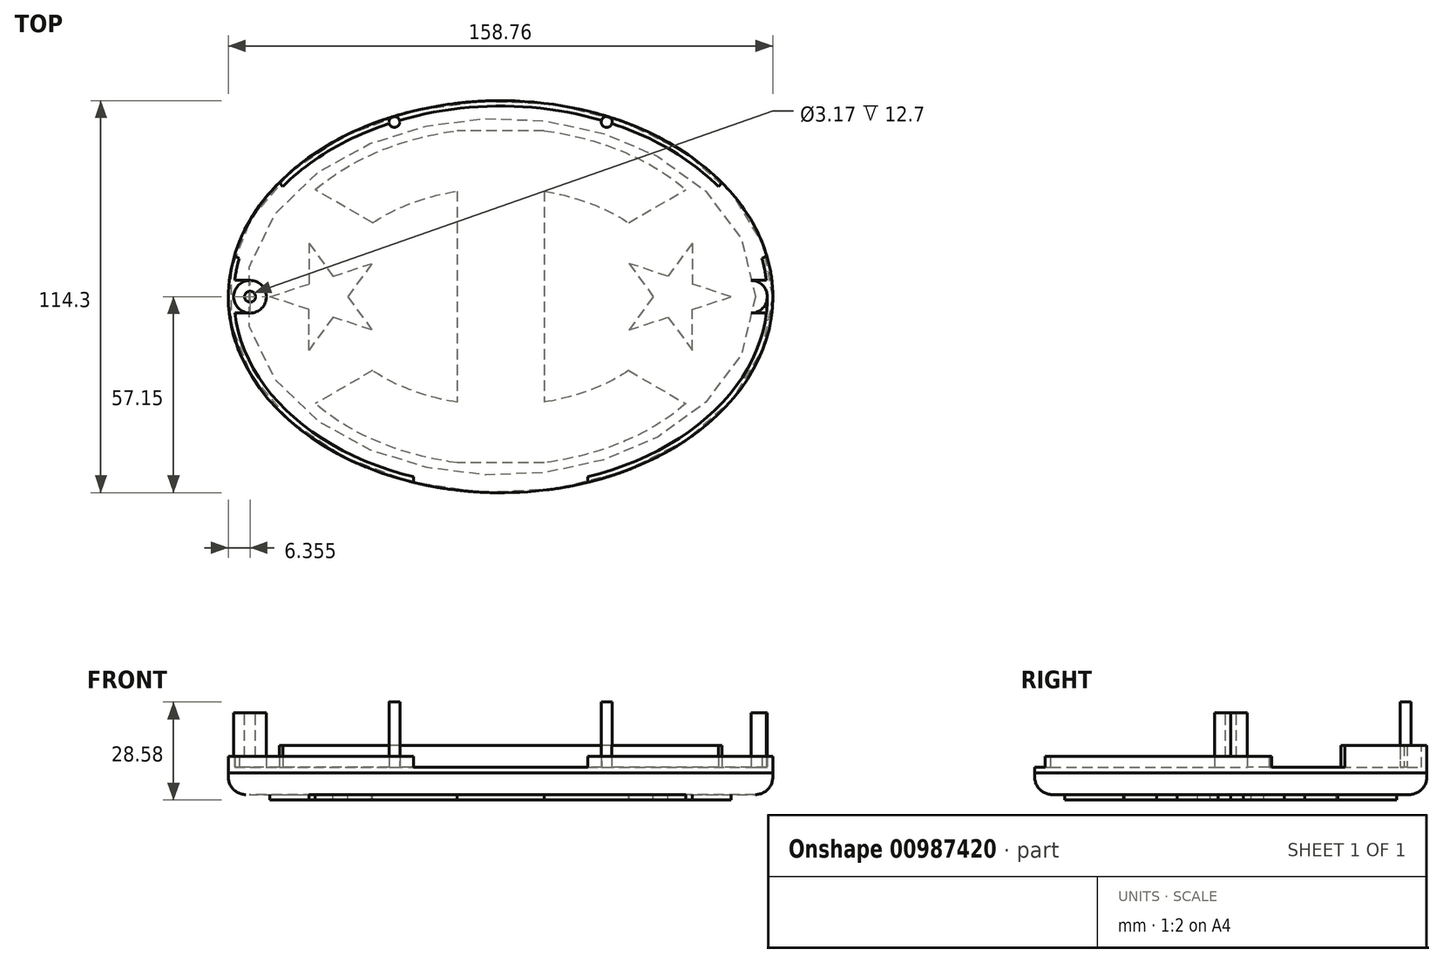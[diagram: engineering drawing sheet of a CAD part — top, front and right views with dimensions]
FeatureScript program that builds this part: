
annotation { "Feature Type Name" : "Feature", "Feature Type Description" : "" }
export const myFeature = defineFeature(function(context is Context, id is Id, definition is map)
    precondition{}
    {
        {
            var Q0;
            Q0=qCreatedBy(makeId("Top.planeOp"),FACE);
            var sketch = newSketch(context, id + "F0", { "sketchPlane" : qUnion([Q0])});
            skEllipse(sketch, "E0", {"center": v(0, 0) * mm, "majorRadius": 79.38 * mm, "minorRadius": 57.15 * mm, "majorAxis": v(1, 0)});
            skSolve(sketch);
        }
        {
            var Q0;
            Q0=makeQuery(id+"F0.imprint","IMPRINT",FACE,{"disambiguationData":[TD([[makeQuery(id+"F0.imprint","IMPRINT",EDGE,{"derivedFrom":sQuery(id+"F0.wireOp",EDGE,"E0")}),1.0]])]});
            extrude(context, id + "F1", {"entities" : qUnion([Q0]), "depth" : 1.59 * mm, "offsetDistance" : 25.4 * mm});
        }
        {
            var Q0;
            Q0=makeQuery(id+"F1.opExtrude","CAP_FACE",FACE,{"disambiguationData":[OSD([sQuery(id+"F0.wireOp",EDGE,"E0")])],"isStart":false});
            var sketch = newSketch(context, id + "F2", { "sketchPlane" : qUnion([Q0])});
            skEllipse(sketch, "E1", {"center": v(0, 0) * mm, "majorRadius": 77.79 * mm, "minorRadius": 55.56 * mm, "majorAxis": v(1, 0)});
            skLineSegment(sketch, "E2", {"start": v(-25.4, -54.14) * mm, "end": v(25.4, -54.14) * mm});
            skLineSegment(sketch, "E3", {"start": v(-25.4, -54.14) * mm, "end": v(-25.4, -52.52) * mm});
            skLineSegment(sketch, "E4", {"start": v(25.4, -54.14) * mm, "end": v(25.4, -52.52) * mm});
            skLineSegment(sketch, "E5", {"start": v(-63.5, 32.1) * mm, "end": v(63.5, 32.1) * mm});
            skLineSegment(sketch, "E6", {"start": v(-64.51, 33.3) * mm, "end": v(-63.5, 32.1) * mm});
            skLineSegment(sketch, "E7", {"start": v(63.5, 32.1) * mm, "end": v(64.51, 33.3) * mm});
            skLineSegment(sketch, "E8", {"start": v(-76.2, 11.17) * mm, "end": v(76.2, 11.17) * mm});
            skLineSegment(sketch, "E9", {"start": v(-76.2, 11.17) * mm, "end": v(-77.61, 11.98) * mm});
            skLineSegment(sketch, "E10", {"start": v(76.2, 11.17) * mm, "end": v(77.61, 11.98) * mm});
            skSolve(sketch);
        }
        {
            var Q0;
            {var subQ0=sQuery(id+"F2.wireOp",EDGE,"E3");Q0=makeQuery(id+"F2.imprint","IMPRINT",FACE,{"disambiguationData":[TD([[makeQuery(id+"F2.imprint","IMPRINT",EDGE,{"derivedFrom":subQ0}),1.0]])]});}
            var Q1;
            {var subQ0=sQuery(id+"F2.wireOp",EDGE,"E4");Q1=makeQuery(id+"F2.imprint","IMPRINT",FACE,{"disambiguationData":[TD([[makeQuery(id+"F2.imprint","IMPRINT",EDGE,{"derivedFrom":subQ0}),-1.0]])]});}
            extrude(context, id + "F3", {"entities" : qUnion([Q0, Q1]), "operationType" : NewBodyOperationType.ADD, "depth" : 3.17 * mm, "offsetDistance" : 25.4 * mm});
        }
        {
            var Q0;
            {var subQ0=sQuery(id+"F2.wireOp",EDGE,"E6");Q0=makeQuery(id+"F2.imprint","IMPRINT",FACE,{"disambiguationData":[TD([[makeQuery(id+"F2.imprint","IMPRINT",EDGE,{"derivedFrom":subQ0}),1.0]])]});}
            extrude(context, id + "F4", {"entities" : qUnion([Q0]), "operationType" : NewBodyOperationType.ADD, "depth" : 6.35 * mm, "offsetDistance" : 25.4 * mm});
        }
        {
            var Q0;
            Q0=makeQuery(id+"F1.opExtrude","CAP_FACE",FACE,{"disambiguationData":[OSD([sQuery(id+"F0.wireOp",EDGE,"E0")])],"isStart":false});
            var sketch = newSketch(context, id + "F5", { "sketchPlane" : qUnion([Q0])});
            skCircle(sketch, "E11", {"center": v(-30.96, 50.96) * mm, "radius": 1.59 * mm});
            skCircle(sketch, "E12", {"center": v(30.96, 50.96) * mm, "radius": 1.59 * mm});
            skPoint(sketch, "E13", {"position": v(-32.54, 50.96) * mm});
            skPoint(sketch, "E14", {"position": v(32.54, 50.96) * mm});
            skLineSegment(sketch, "E15", {"start": v(-30.96, 50.96) * mm, "end": v(30.96, 50.96) * mm, "construction": true});
            skPoint(sketch, "E16", {"position": v(0, 50.96) * mm});
            skSolve(sketch);
        }
        {
            var Q0;
            {var subQ0=sQuery(id+"F5.wireOp",EDGE,"E11");var subQ1=makeQuery(id+"F4.opExtrude","CAP_EDGE",EDGE,{"disambiguationData":[OSD([sQuery(id+"F2.wireOp",EDGE,"E1")])],"isStart":true});var subQ2=makeQuery(id+"F5.imprint","INTERSECT",VERTEX,{"disambiguationData":[OD(0.0)],"derivedFrom":[subQ1,subQ0]});Q0=makeQuery(id+"F5.imprint","IMPRINT",FACE,{"disambiguationData":[TD([[makeQuery(id+"F5.imprint","IMPRINT",EDGE,{"disambiguationData":[TD([[subQ2,-1.0]])],"derivedFrom":subQ0}),1.0]])]});}
            var Q1;
            {var subQ0=sQuery(id+"F5.wireOp",EDGE,"E12");var subQ1=makeQuery(id+"F4.opExtrude","CAP_EDGE",EDGE,{"disambiguationData":[OSD([sQuery(id+"F2.wireOp",EDGE,"E1")])],"isStart":true});var subQ2=makeQuery(id+"F5.imprint","INTERSECT",VERTEX,{"disambiguationData":[OD(0.0)],"derivedFrom":[subQ1,subQ0]});Q1=makeQuery(id+"F5.imprint","IMPRINT",FACE,{"disambiguationData":[TD([[makeQuery(id+"F5.imprint","IMPRINT",EDGE,{"disambiguationData":[TD([[subQ2,1.0]])],"derivedFrom":subQ0}),1.0]])]});}
            var Q2;
            {var subQ0=sQuery(id+"F5.wireOp",EDGE,"E11");var subQ1=makeQuery(id+"F4.opExtrude","CAP_EDGE",EDGE,{"disambiguationData":[OSD([sQuery(id+"F2.wireOp",EDGE,"E1")])],"isStart":true});var subQ2=makeQuery(id+"F5.imprint","INTERSECT",VERTEX,{"disambiguationData":[OD(0.0)],"derivedFrom":[subQ1,subQ0]});Q2=makeQuery(id+"F5.imprint","IMPRINT",FACE,{"disambiguationData":[TD([[makeQuery(id+"F5.imprint","IMPRINT",EDGE,{"disambiguationData":[TD([[subQ2,1.0]])],"derivedFrom":subQ0}),1.0]])]});}
            var Q3;
            {var subQ0=sQuery(id+"F5.wireOp",EDGE,"E12");var subQ1=makeQuery(id+"F4.opExtrude","CAP_EDGE",EDGE,{"disambiguationData":[OSD([sQuery(id+"F2.wireOp",EDGE,"E1")])],"isStart":true});var subQ2=makeQuery(id+"F5.imprint","INTERSECT",VERTEX,{"disambiguationData":[OD(0.0)],"derivedFrom":[subQ1,subQ0]});Q3=makeQuery(id+"F5.imprint","IMPRINT",FACE,{"disambiguationData":[TD([[makeQuery(id+"F5.imprint","IMPRINT",EDGE,{"disambiguationData":[TD([[subQ2,-1.0]])],"derivedFrom":subQ0}),1.0]])]});}
            extrude(context, id + "F6", {"entities" : qUnion([Q0, Q1, Q2, Q3]), "operationType" : NewBodyOperationType.ADD, "depth" : 19.05 * mm, "offsetDistance" : 25.4 * mm});
        }
        {
            var Q0;
            Q0=makeQuery(id+"F1.opExtrude","CAP_FACE",FACE,{"disambiguationData":[OSD([sQuery(id+"F0.wireOp",EDGE,"E0")])],"isStart":false});
            var sketch = newSketch(context, id + "F7", { "sketchPlane" : qUnion([Q0])});
            skCircle(sketch, "E17", {"center": v(-73.03, 0) * mm, "radius": 4.76 * mm});
            skLineSegment(sketch, "E18", {"start": v(-73.03, -4.76) * mm, "end": v(-77.5, -4.76) * mm});
            skLineSegment(sketch, "E19", {"start": v(-73.03, 4.76) * mm, "end": v(-77.5, 4.76) * mm});
            skEllipticalArc(sketch, "E20.0", {});
            skPoint(sketch, "E21.orphan", {"position": v(-76.2, 11.17) * mm});
            skPoint(sketch, "E22.orphan", {"position": v(-25.4, -52.52) * mm});
            skLineSegment(sketch, "E23", {"start": v(0, 0) * mm, "end": v(0, 25.4) * mm, "construction": true});
            skEllipticalArc(sketch, "E24.MirrorCS", {});
            skLineSegment(sketch, "E25.MirrorCS", {"start": v(73.03, 4.76) * mm, "end": v(77.5, 4.76) * mm});
            skCircle(sketch, "E26.MirrorC", {"center": v(73.03, 0) * mm, "radius": 4.76 * mm});
            skLineSegment(sketch, "E27.MirrorCS", {"start": v(73.03, -4.76) * mm, "end": v(77.5, -4.76) * mm});
            const initialGuessF7  = {"E20.0": [0, 0, 1, 0, 0.07778750000000001, 0.05556250000000001, 3.0557730630838975, 3.2274122440956874], "E24.MirrorCS": [0, 0, -1, 0, 0.07778750000000001, 0.05556250000000001, 3.0557730630838993, 3.2274122440956887]};
            skSetInitialGuess(sketch, initialGuessF7);
            skSolve(sketch);
        }
        {
            var Q0;
            {var subQ0=sQuery(id+"F7.wireOp",EDGE,"E19");Q0=makeQuery(id+"F7.imprint","IMPRINT",FACE,{"disambiguationData":[TD([[makeQuery(id+"F7.imprint","IMPRINT",EDGE,{"derivedFrom":subQ0}),1.0]])]});}
            var Q1;
            {var subQ0=sQuery(id+"F7.wireOp",EDGE,"E18");Q1=makeQuery(id+"F7.imprint","IMPRINT",FACE,{"disambiguationData":[TD([[makeQuery(id+"F7.imprint","IMPRINT",EDGE,{"derivedFrom":subQ0}),-1.0]])]});}
            var Q2;
            {var subQ0=sQuery(id+"F7.wireOp",EDGE,"E17");var subQ1=makeQuery(id+"F7.imprint","INTERSECT",VERTEX,{"derivedFrom":[subQ0,sQuery(id+"F7.wireOp",EDGE,"E19")]});Q2=makeQuery(id+"F7.imprint","IMPRINT",FACE,{"disambiguationData":[TD([[makeQuery(id+"F7.imprint","IMPRINT",EDGE,{"disambiguationData":[TD([[subQ1,-1.0]])],"derivedFrom":subQ0}),1.0]])]});}
            var Q3;
            {var subQ0=sQuery(id+"F7.wireOp",EDGE,"E26.MirrorC");var subQ1=makeQuery(id+"F7.imprint","INTERSECT",VERTEX,{"derivedFrom":[sQuery(id+"F7.wireOp",EDGE,"E24.MirrorCS"),subQ0]});Q3=makeQuery(id+"F7.imprint","IMPRINT",FACE,{"disambiguationData":[TD([[makeQuery(id+"F7.imprint","IMPRINT",EDGE,{"disambiguationData":[TD([[subQ1,1.0]])],"derivedFrom":subQ0}),-1.0]])]});}
            var Q4;
            {var subQ3=sQuery(id+"F7.wireOp",EDGE,"E25.MirrorCS");Q4=makeQuery(id+"F7.imprint","IMPRINT",FACE,{"disambiguationData":[TD([[makeQuery(id+"F7.imprint","IMPRINT",EDGE,{"derivedFrom":subQ3}),-1.0]])]});}
            var Q5;
            {var subQ3=sQuery(id+"F7.wireOp",EDGE,"E27.MirrorCS");Q5=makeQuery(id+"F7.imprint","IMPRINT",FACE,{"disambiguationData":[TD([[makeQuery(id+"F7.imprint","IMPRINT",EDGE,{"derivedFrom":subQ3}),1.0]])]});}
            extrude(context, id + "F8", {"entities" : qUnion([Q0, Q1, Q2, Q3, Q4, Q5]), "operationType" : NewBodyOperationType.ADD, "depth" : 3.17 * mm, "offsetDistance" : 25.4 * mm});
        }
        {
            var Q0;
            {var subQ0=sQuery(id+"F7.wireOp",EDGE,"E17");var subQ1=makeQuery(id+"F7.imprint","INTERSECT",VERTEX,{"derivedFrom":[subQ0,sQuery(id+"F7.wireOp",EDGE,"E19")]});Q0=makeQuery(id+"F7.imprint","IMPRINT",FACE,{"disambiguationData":[TD([[makeQuery(id+"F7.imprint","IMPRINT",EDGE,{"disambiguationData":[TD([[subQ1,-1.0]])],"derivedFrom":subQ0}),1.0]])]});}
            var Q1;
            {var subQ0=sQuery(id+"F7.wireOp",EDGE,"E26.MirrorC");var subQ1=makeQuery(id+"F7.imprint","INTERSECT",VERTEX,{"derivedFrom":[sQuery(id+"F7.wireOp",EDGE,"E24.MirrorCS"),subQ0]});Q1=makeQuery(id+"F7.imprint","IMPRINT",FACE,{"disambiguationData":[TD([[makeQuery(id+"F7.imprint","IMPRINT",EDGE,{"disambiguationData":[TD([[subQ1,1.0]])],"derivedFrom":subQ0}),-1.0]])]});}
            extrude(context, id + "F9", {"entities" : qUnion([Q0, Q1]), "operationType" : NewBodyOperationType.ADD, "depth" : 15.88 * mm, "offsetDistance" : 25.4 * mm});
        }
        {
            var Q0;
            Q0=makeQuery(id+"F9.opExtrude","CAP_FACE",FACE,{"disambiguationData":[OSD([sQuery(id+"F7.wireOp",EDGE,"E17")])],"isStart":false});
            var sketch = newSketch(context, id + "F10", { "sketchPlane" : qUnion([Q0])});
            skCircle(sketch, "E28", {"center": v(-73.03, 0) * mm, "radius": 1.59 * mm});
            skPoint(sketch, "E29", {"position": v(73.03, 0) * mm});
            skCircle(sketch, "E30", {"center": v(73.03, 0) * mm, "radius": 1.59 * mm});
            skSolve(sketch);
        }
        {
            var Q0;
            Q0=makeQuery(id+"F10.imprint","IMPRINT",FACE,{"disambiguationData":[TD([[makeQuery(id+"F10.imprint","IMPRINT",EDGE,{"derivedFrom":sQuery(id+"F10.wireOp",EDGE,"E28")}),1.0]])]});
            var Q1;
            Q1=makeQuery(id+"F10.imprint","IMPRINT",FACE,{"disambiguationData":[TD([[makeQuery(id+"F10.imprint","IMPRINT",EDGE,{"derivedFrom":sQuery(id+"F10.wireOp",EDGE,"E30")}),1.0]])]});
            extrude(context, id + "F11", {"entities" : qUnion([Q0, Q1]), "operationType" : NewBodyOperationType.REMOVE, "oppositeDirection" : true, "depth" : 12.7 * mm, "offsetDistance" : 25.4 * mm});
        }
        {
            var Q0;
            Q0=makeQuery(id+"F1.opExtrude","CAP_FACE",FACE,{"disambiguationData":[OSD([sQuery(id+"F0.wireOp",EDGE,"E0")])],"isStart":true});
            var sketch = newSketch(context, id + "F12", { "sketchPlane" : qUnion([Q0])});
            skEllipse(sketch, "E31.0.0", {"center": v(0, 0) * mm, "majorRadius": 79.38 * mm, "minorRadius": 57.15 * mm, "majorAxis": v(1, 0)});
            skSolve(sketch);
        }
        {
            var Q0;
            Q0 = qSketchRegion(id + "F12", true);
            extrude(context, id + "F13", {"entities" : qUnion([Q0]), "depth" : 6.35 * mm, "offsetDistance" : 25.4 * mm});
        }
        {
            var Q0;
            Q0=makeQuery(id+"F13.opExtrude","CAP_EDGE",EDGE,{"disambiguationData":[OSD([sQuery(id+"F12.wireOp",EDGE,"E31.0.0")])],"isStart":false});
            fillet(context, id + "F14", {"entities" : qUnion([Q0]), "radius" : 5.08 * mm, "tangentPropagation" : true, "allowEdgeOverflow" : false});
        }
        {
            var Q0;
            Q0=makeQuery(id+"F13.opExtrude","CAP_FACE",FACE,{"disambiguationData":[OSD([sQuery(id+"F12.wireOp",EDGE,"E31.0.0")])],"isStart":false});
            var sketch = newSketch(context, id + "F15", { "sketchPlane" : qUnion([Q0])});
            skPoint(sketch, "E32", {"position": v(34.39, 39.1) * mm});
            skPoint(sketch, "E33", {"position": v(38.93, 32.43) * mm});
            skPoint(sketch, "E34", {"position": v(42, 25.2) * mm});
            skPoint(sketch, "E35", {"position": v(44.9, 15.35) * mm});
            skPoint(sketch, "E36", {"position": v(46.32, 4.56) * mm});
            skPoint(sketch, "E37", {"position": v(47.2, -7.17) * mm});
            skPoint(sketch, "E38", {"position": v(46.9, -15.38) * mm});
            skPoint(sketch, "E39", {"position": v(44.76, -23.97) * mm});
            skPoint(sketch, "E40", {"position": v(41.67, -31.08) * mm});
            skPoint(sketch, "E41", {"position": v(37.64, -37.83) * mm});
            skPoint(sketch, "E42", {"position": v(30.8, -44.05) * mm});
            skPoint(sketch, "E43", {"position": v(23.18, -46) * mm});
            skPoint(sketch, "E44", {"position": v(13.85, -46) * mm});
            skPoint(sketch, "E45", {"position": v(8.76, -41.5) * mm});
            skPoint(sketch, "E46", {"position": v(7.4, -35.36) * mm});
            skPoint(sketch, "E47", {"position": v(9.76, -29.55) * mm});
            skPoint(sketch, "E48", {"position": v(15.32, -26.33) * mm});
            skPoint(sketch, "E49", {"position": v(19.78, -25.54) * mm});
            skPoint(sketch, "E50", {"position": v(25.57, -25.66) * mm});
            skPoint(sketch, "E51", {"position": v(28.75, -26.93) * mm});
            skPoint(sketch, "E52", {"position": v(31, -27.28) * mm});
            skPoint(sketch, "E53", {"position": v(32.82, -23.72) * mm});
            skPoint(sketch, "E54", {"position": v(34.06, -17.75) * mm});
            skPoint(sketch, "E55", {"position": v(34.2, -12.9) * mm});
            skPoint(sketch, "E56", {"position": v(33.4, -8.8) * mm});
            skPoint(sketch, "E57", {"position": v(32.06, -4.72) * mm});
            skPoint(sketch, "E58", {"position": v(29.94, 1.22) * mm});
            skPoint(sketch, "E59", {"position": v(26.93, 3.42) * mm});
            skPoint(sketch, "E60", {"position": v(23.18, -0.34) * mm});
            skPoint(sketch, "E61", {"position": v(18.25, -4.3) * mm});
            skPoint(sketch, "E62", {"position": v(11.38, -7.18) * mm});
            skPoint(sketch, "E63", {"position": v(3.38, -9.12) * mm});
            skPoint(sketch, "E64", {"position": v(-4.82, -9.77) * mm});
            skPoint(sketch, "E65", {"position": v(-12.3, -7.98) * mm});
            skPoint(sketch, "E66", {"position": v(-16.8, -6.35) * mm});
            skPoint(sketch, "E67", {"position": v(-21.69, 0) * mm});
            skPoint(sketch, "E68", {"position": v(-25.84, 2.12) * mm});
            skPoint(sketch, "E69", {"position": v(-29.04, 4.51) * mm});
            skPoint(sketch, "E70", {"position": v(-35.39, 5.56) * mm});
            skPoint(sketch, "E71", {"position": v(-32.97, 23.1) * mm});
            skPoint(sketch, "E72", {"position": v(-30.19, 24.81) * mm});
            skPoint(sketch, "E73", {"position": v(-28.56, 29.86) * mm});
            skPoint(sketch, "E74", {"position": v(-30.19, 34.33) * mm});
            skPoint(sketch, "E75", {"position": v(-32.97, 38.96) * mm});
            skPoint(sketch, "E76", {"position": v(-32.53, 43.33) * mm});
            skPoint(sketch, "E77", {"position": v(-28.9, 44.58) * mm});
            skPoint(sketch, "E78", {"position": v(31.7, 41.92) * mm});
            skPoint(sketch, "E79", {"position": v(26.4, 43.84) * mm});
            skPoint(sketch, "E80", {"position": v(21.5, 45.23) * mm});
            skPoint(sketch, "E81", {"position": v(18.62, 44.02) * mm});
            skPoint(sketch, "E82", {"position": v(17.5, 38.08) * mm});
            skPoint(sketch, "E83", {"position": v(17.67, 34) * mm});
            skPoint(sketch, "E84", {"position": v(18.78, 28.47) * mm});
            skPoint(sketch, "E85", {"position": v(18.02, 25.57) * mm});
            skPoint(sketch, "E86", {"position": v(14.3, 28.03) * mm});
            skPoint(sketch, "E87", {"position": v(9.27, 29.95) * mm});
            skPoint(sketch, "E88", {"position": v(4.38, 31.09) * mm});
            skPoint(sketch, "E89", {"position": v(0, 31.56) * mm});
            skPoint(sketch, "E90", {"position": v(-6.97, 31.63) * mm});
            skPoint(sketch, "E91", {"position": v(-12.9, 31.04) * mm});
            skPoint(sketch, "E92", {"position": v(-20.98, 46.24) * mm});
            skPoint(sketch, "E93", {"position": v(-17.93, 45.22) * mm});
            skPoint(sketch, "E94", {"position": v(-14.43, 38.66) * mm});
            skPoint(sketch, "E95", {"position": v(-25.26, 45.9) * mm});
            skPoint(sketch, "E96", {"position": v(-37.95, 1.3) * mm});
            skPoint(sketch, "E97", {"position": v(-38.05, -14) * mm});
            skPoint(sketch, "E98", {"position": v(-34.8, -21.34) * mm});
            skPoint(sketch, "E99", {"position": v(-48.3, -16.47) * mm});
            skPoint(sketch, "E100", {"position": v(-49.5, 0) * mm});
            skPoint(sketch, "E101", {"position": v(-47.8, 10.15) * mm});
            skPoint(sketch, "E102", {"position": v(-42.09, 18.38) * mm});
            skPoint(sketch, "E103", {"position": v(-39.71, -6.63) * mm});
            skPoint(sketch, "E104", {"position": v(-42.13, -28.7) * mm});
            skPoint(sketch, "E105", {"position": v(-33.45, -37.55) * mm});
            skPoint(sketch, "E106", {"position": v(-30.65, -37.9) * mm});
            skPoint(sketch, "E107", {"position": v(-29, -36) * mm});
            skPoint(sketch, "E108", {"position": v(-32.07, -27.28) * mm});
            skLineSegment(sketch, "E109", {"start": v(37.64, -37.83) * mm, "end": v(41.67, -31.08) * mm});
            skLineSegment(sketch, "E110", {"start": v(44.76, -23.97) * mm, "end": v(46.9, -15.38) * mm});
            skLineSegment(sketch, "E111", {"start": v(47.2, -7.17) * mm, "end": v(46.32, 4.56) * mm});
            skLineSegment(sketch, "E112", {"start": v(44.9, 15.35) * mm, "end": v(42, 25.2) * mm});
            skLineSegment(sketch, "E113", {"start": v(44.9, 15.35) * mm, "end": v(46.32, 4.56) * mm});
            skLineSegment(sketch, "E114", {"start": v(47.2, -7.17) * mm, "end": v(46.9, -15.38) * mm});
            skLineSegment(sketch, "E115", {"start": v(44.76, -23.97) * mm, "end": v(41.67, -31.08) * mm});
            skLineSegment(sketch, "E116", {"start": v(37.64, -37.83) * mm, "end": v(30.8, -44.05) * mm});
            skLineSegment(sketch, "E117", {"start": v(30.8, -44.05) * mm, "end": v(23.18, -46) * mm});
            skLineSegment(sketch, "E118", {"start": v(23.18, -46) * mm, "end": v(13.85, -46) * mm});
            skLineSegment(sketch, "E119", {"start": v(13.85, -46) * mm, "end": v(8.76, -41.5) * mm});
            skLineSegment(sketch, "E120", {"start": v(8.76, -41.5) * mm, "end": v(7.4, -35.36) * mm});
            skLineSegment(sketch, "E121", {"start": v(7.4, -35.36) * mm, "end": v(9.76, -29.55) * mm});
            skLineSegment(sketch, "E122", {"start": v(9.76, -29.55) * mm, "end": v(15.32, -26.33) * mm});
            skLineSegment(sketch, "E123", {"start": v(19.78, -25.54) * mm, "end": v(15.32, -26.33) * mm});
            skLineSegment(sketch, "E124", {"start": v(19.78, -25.54) * mm, "end": v(25.57, -25.66) * mm});
            skLineSegment(sketch, "E125", {"start": v(28.75, -26.93) * mm, "end": v(25.57, -25.66) * mm});
            skLineSegment(sketch, "E126", {"start": v(28.75, -26.93) * mm, "end": v(31, -27.28) * mm});
            skLineSegment(sketch, "E127", {"start": v(31, -27.28) * mm, "end": v(32.82, -23.72) * mm});
            skLineSegment(sketch, "E128", {"start": v(32.82, -23.72) * mm, "end": v(34.06, -17.75) * mm});
            skLineSegment(sketch, "E129", {"start": v(34.06, -17.75) * mm, "end": v(34.2, -12.9) * mm});
            skLineSegment(sketch, "E130", {"start": v(33.4, -8.8) * mm, "end": v(34.2, -12.9) * mm});
            skLineSegment(sketch, "E131", {"start": v(33.4, -8.8) * mm, "end": v(32.06, -4.72) * mm});
            skLineSegment(sketch, "E132", {"start": v(32.06, -4.72) * mm, "end": v(29.94, 1.22) * mm});
            skLineSegment(sketch, "E133", {"start": v(29.94, 1.22) * mm, "end": v(26.93, 3.42) * mm});
            skLineSegment(sketch, "E134", {"start": v(26.93, 3.42) * mm, "end": v(23.18, -0.34) * mm});
            skLineSegment(sketch, "E135", {"start": v(23.18, -0.34) * mm, "end": v(18.25, -4.3) * mm});
            skLineSegment(sketch, "E136", {"start": v(18.25, -4.3) * mm, "end": v(11.38, -7.18) * mm});
            skLineSegment(sketch, "E137", {"start": v(3.38, -9.12) * mm, "end": v(11.38, -7.18) * mm});
            skLineSegment(sketch, "E138", {"start": v(3.38, -9.12) * mm, "end": v(-4.82, -9.77) * mm});
            skLineSegment(sketch, "E139", {"start": v(-4.82, -9.77) * mm, "end": v(-12.3, -7.98) * mm});
            skLineSegment(sketch, "E140", {"start": v(-12.3, -8) * mm, "end": v(-16.8, -6.35) * mm});
            skLineSegment(sketch, "E141", {"start": v(-21.69, 0) * mm, "end": v(-16.8, -6.35) * mm});
            skLineSegment(sketch, "E142", {"start": v(-21.69, 0) * mm, "end": v(-25.84, 2.12) * mm});
            skLineSegment(sketch, "E143", {"start": v(-25.84, 2.12) * mm, "end": v(-29.04, 4.51) * mm});
            skLineSegment(sketch, "E144", {"start": v(-35.39, 5.56) * mm, "end": v(-37.95, 1.3) * mm});
            skLineSegment(sketch, "E145", {"start": v(-39.71, -6.63) * mm, "end": v(-38.05, -14) * mm});
            skLineSegment(sketch, "E146", {"start": v(-34.8, -21.34) * mm, "end": v(-32.07, -27.28) * mm});
            skLineSegment(sketch, "E147", {"start": v(-29, -36) * mm, "end": v(-30.65, -37.9) * mm});
            skLineSegment(sketch, "E148", {"start": v(-33.45, -37.55) * mm, "end": v(-42.13, -28.7) * mm});
            skLineSegment(sketch, "E149", {"start": v(-48.3, -16.47) * mm, "end": v(-49.5, 0) * mm});
            skLineSegment(sketch, "E150", {"start": v(-47.8, 10.15) * mm, "end": v(-42.09, 18.38) * mm});
            skLineSegment(sketch, "E151", {"start": v(-47.8, 10.15) * mm, "end": v(-49.5, 0) * mm});
            skLineSegment(sketch, "E152", {"start": v(-37.95, 1.3) * mm, "end": v(-39.71, -6.63) * mm});
            skLineSegment(sketch, "E153", {"start": v(-38.05, -14) * mm, "end": v(-34.8, -21.34) * mm});
            skLineSegment(sketch, "E154", {"start": v(-32.07, -27.28) * mm, "end": v(-29, -36) * mm});
            skLineSegment(sketch, "E155", {"start": v(-30.65, -37.9) * mm, "end": v(-33.45, -37.55) * mm});
            skLineSegment(sketch, "E156", {"start": v(-42.13, -28.7) * mm, "end": v(-48.3, -16.47) * mm});
            skLineSegment(sketch, "E157", {"start": v(42, 25.2) * mm, "end": v(38.93, 32.43) * mm});
            skLineSegment(sketch, "E158", {"start": v(34.39, 39.1) * mm, "end": v(31.7, 41.92) * mm});
            skLineSegment(sketch, "E159", {"start": v(26.4, 43.84) * mm, "end": v(21.5, 45.23) * mm});
            skLineSegment(sketch, "E160", {"start": v(18.62, 44.02) * mm, "end": v(17.5, 38.08) * mm});
            skLineSegment(sketch, "E161", {"start": v(17.67, 34) * mm, "end": v(18.78, 28.47) * mm});
            skLineSegment(sketch, "E162", {"start": v(18.02, 25.57) * mm, "end": v(14.3, 28.03) * mm});
            skLineSegment(sketch, "E163", {"start": v(9.27, 29.95) * mm, "end": v(4.38, 31.09) * mm});
            skLineSegment(sketch, "E164", {"start": v(0, 31.56) * mm, "end": v(-6.97, 31.63) * mm});
            skLineSegment(sketch, "E165", {"start": v(-14.43, 38.66) * mm, "end": v(-17.93, 45.22) * mm});
            skLineSegment(sketch, "E166", {"start": v(-6.97, 31.63) * mm, "end": v(-12.9, 31.04) * mm});
            skLineSegment(sketch, "E167", {"start": v(0, 31.56) * mm, "end": v(4.38, 31.09) * mm});
            skLineSegment(sketch, "E168", {"start": v(9.27, 29.95) * mm, "end": v(14.3, 28.03) * mm});
            skLineSegment(sketch, "E169", {"start": v(18.02, 25.57) * mm, "end": v(18.78, 28.47) * mm});
            skLineSegment(sketch, "E170", {"start": v(17.67, 34) * mm, "end": v(17.5, 38.08) * mm});
            skLineSegment(sketch, "E171", {"start": v(18.62, 44.02) * mm, "end": v(21.5, 45.23) * mm});
            skLineSegment(sketch, "E172", {"start": v(26.4, 43.84) * mm, "end": v(31.7, 41.92) * mm});
            skLineSegment(sketch, "E173", {"start": v(34.39, 39.1) * mm, "end": v(38.93, 32.43) * mm});
            skLineSegment(sketch, "E174", {"start": v(-17.93, 45.22) * mm, "end": v(-20.98, 46.24) * mm});
            skLineSegment(sketch, "E175", {"start": v(-25.26, 45.9) * mm, "end": v(-28.9, 44.58) * mm});
            skLineSegment(sketch, "E176", {"start": v(-32.53, 43.33) * mm, "end": v(-32.97, 38.96) * mm});
            skLineSegment(sketch, "E177", {"start": v(-32.97, 38.96) * mm, "end": v(-30.19, 34.33) * mm});
            skLineSegment(sketch, "E178", {"start": v(-28.56, 29.86) * mm, "end": v(-30.19, 24.81) * mm});
            skLineSegment(sketch, "E179", {"start": v(-32.97, 23.1) * mm, "end": v(-42.09, 18.38) * mm});
            skLineSegment(sketch, "E180", {"start": v(-32.97, 23.1) * mm, "end": v(-30.19, 24.81) * mm});
            skLineSegment(sketch, "E181", {"start": v(-28.56, 29.86) * mm, "end": v(-30.19, 34.33) * mm});
            skLineSegment(sketch, "E182", {"start": v(-32.53, 43.33) * mm, "end": v(-28.9, 44.58) * mm});
            skLineSegment(sketch, "E183", {"start": v(-25.26, 45.9) * mm, "end": v(-20.98, 46.24) * mm});
            skLineSegment(sketch, "E184", {"start": v(-12.9, 31.04) * mm, "end": v(-14.43, 38.66) * mm});
            skLineSegment(sketch, "E185", {"start": v(-29.04, 4.51) * mm, "end": v(-35.39, 5.56) * mm});
            skSolve(sketch);
        }
        {
            var Q0;
            Q0=makeQuery(id+"F13.opExtrude","CAP_FACE",FACE,{"disambiguationData":[OSD([sQuery(id+"F12.wireOp",EDGE,"E31.0.0")])],"isStart":false});
            var sketch = newSketch(context, id + "F16", { "sketchPlane" : qUnion([Q0])});
            skEllipse(sketch, "E186", {"center": v(0, 0) * mm, "majorRadius": 69.85 * mm, "minorRadius": 49.21 * mm, "majorAxis": v(-1, 0)});
            skLineSegment(sketch, "E187", {"start": v(0, 0) * mm, "end": v(54.03, -31.2) * mm});
            skLineSegment(sketch, "E188", {"start": v(0, 0) * mm, "end": v(-54.03, -31.2) * mm});
            skEllipse(sketch, "E189", {"center": v(0, 0) * mm, "majorRadius": 50.8 * mm, "minorRadius": 31.75 * mm, "majorAxis": v(-1, 0)});
            skLineSegment(sketch, "E190", {"start": v(0, 0) * mm, "end": v(0, -49.21) * mm, "construction": true});
            skLineSegment(sketch, "E191", {"start": v(0, 0) * mm, "end": v(54.03, 31.2) * mm});
            skLineSegment(sketch, "E192", {"start": v(0, 0) * mm, "end": v(-54.03, 31.2) * mm});
            skLineSegment(sketch, "E193.bottom", {"start": v(12.7, -48.4) * mm, "end": v(-12.7, -48.4) * mm});
            skLineSegment(sketch, "E193.top", {"start": v(12.7, 48.4) * mm, "end": v(-12.7, 48.4) * mm});
            skLineSegment(sketch, "E193.left", {"start": v(12.7, -48.4) * mm, "end": v(12.7, 48.4) * mm});
            skLineSegment(sketch, "E193.right", {"start": v(-12.7, -48.4) * mm, "end": v(-12.7, 48.4) * mm});
            skPoint(sketch, "E194", {"position": v(0, -48.4) * mm});
            skSolve(sketch);
        }
        {
            var Q0;
            {var subQ0=sQuery(id+"F16.wireOp",EDGE,"E187");var subQ1=sQuery(id+"F16.wireOp",EDGE,"E186");var subQ2=makeQuery(id+"F16.imprint","INTERSECT",VERTEX,{"derivedFrom":[subQ1,subQ0]});Q0=makeQuery(id+"F16.imprint","IMPRINT",FACE,{"disambiguationData":[TD([[makeQuery(id+"F16.imprint","IMPRINT",EDGE,{"disambiguationData":[TD([[subQ2,1.0]])],"derivedFrom":subQ0}),-1.0]])]});}
            var Q1;
            {var subQ0=sQuery(id+"F16.wireOp",EDGE,"E188");var subQ1=sQuery(id+"F16.wireOp",EDGE,"E186");var subQ2=makeQuery(id+"F16.imprint","INTERSECT",VERTEX,{"derivedFrom":[subQ1,subQ0]});Q1=makeQuery(id+"F16.imprint","IMPRINT",FACE,{"disambiguationData":[TD([[makeQuery(id+"F16.imprint","IMPRINT",EDGE,{"disambiguationData":[TD([[subQ2,1.0]])],"derivedFrom":subQ0}),1.0]])]});}
            var Q2;
            {var subQ0=sQuery(id+"F16.wireOp",EDGE,"E193.right");var subQ1=sQuery(id+"F16.wireOp",EDGE,"E189");var subQ2=makeQuery(id+"F16.imprint","INTERSECT",VERTEX,{"disambiguationData":[OD(0.0)],"derivedFrom":[subQ1,subQ0]});Q2=makeQuery(id+"F16.imprint","IMPRINT",FACE,{"disambiguationData":[TD([[makeQuery(id+"F16.imprint","IMPRINT",EDGE,{"disambiguationData":[TD([[subQ2,-1.0]])],"derivedFrom":subQ1}),1.0]])]});}
            var Q3;
            {var subQ0=sQuery(id+"F16.wireOp",EDGE,"E193.left");var subQ1=sQuery(id+"F16.wireOp",EDGE,"E189");var subQ2=makeQuery(id+"F16.imprint","INTERSECT",VERTEX,{"disambiguationData":[OD(1.0)],"derivedFrom":[subQ1,subQ0]});Q3=makeQuery(id+"F16.imprint","IMPRINT",FACE,{"disambiguationData":[TD([[makeQuery(id+"F16.imprint","IMPRINT",EDGE,{"disambiguationData":[TD([[subQ2,-1.0]])],"derivedFrom":subQ1}),1.0]])]});}
            var Q4;
            {var subQ5=sQuery(id+"F16.wireOp",EDGE,"E193.top");Q4=makeQuery(id+"F16.imprint","IMPRINT",FACE,{"disambiguationData":[TD([[makeQuery(id+"F16.imprint","IMPRINT",EDGE,{"derivedFrom":subQ5}),1.0]])]});}
            var Q5;
            {var subQ0=sQuery(id+"F16.wireOp",EDGE,"E191");var subQ5=sQuery(id+"F16.wireOp",EDGE,"E189");var subQ6=makeQuery(id+"F16.imprint","INTERSECT",VERTEX,{"derivedFrom":[subQ5,subQ0]});Q5=makeQuery(id+"F16.imprint","IMPRINT",FACE,{"disambiguationData":[TD([[makeQuery(id+"F16.imprint","IMPRINT",EDGE,{"disambiguationData":[TD([[subQ6,-1.0]])],"derivedFrom":subQ5}),-1.0]])]});}
            var Q6;
            {var subQ3=sQuery(id+"F16.wireOp",EDGE,"E193.right");var subQ5=sQuery(id+"F16.wireOp",EDGE,"E189");var subQ6=makeQuery(id+"F16.imprint","INTERSECT",VERTEX,{"disambiguationData":[OD(1.0)],"derivedFrom":[subQ5,subQ3]});Q6=makeQuery(id+"F16.imprint","IMPRINT",FACE,{"disambiguationData":[TD([[makeQuery(id+"F16.imprint","IMPRINT",EDGE,{"disambiguationData":[TD([[subQ6,-1.0]])],"derivedFrom":subQ5}),-1.0]])]});}
            var Q7;
            {var subQ5=sQuery(id+"F16.wireOp",EDGE,"E193.bottom");Q7=makeQuery(id+"F16.imprint","IMPRINT",FACE,{"disambiguationData":[TD([[makeQuery(id+"F16.imprint","IMPRINT",EDGE,{"derivedFrom":subQ5}),-1.0]])]});}
            var Q8;
            {var subQ1=sQuery(id+"F16.wireOp",EDGE,"E188");var subQ3=sQuery(id+"F16.wireOp",EDGE,"E193.right");var subQ4=makeQuery(id+"F16.imprint","INTERSECT",VERTEX,{"derivedFrom":[subQ1,subQ3]});Q8=makeQuery(id+"F16.imprint","IMPRINT",FACE,{"disambiguationData":[TD([[makeQuery(id+"F16.imprint","IMPRINT",EDGE,{"disambiguationData":[TD([[subQ4,-1.0]])],"derivedFrom":subQ3}),-1.0]])]});}
            var Q9;
            {var subQ1=sQuery(id+"F16.wireOp",EDGE,"E187");var subQ3=sQuery(id+"F16.wireOp",EDGE,"E193.left");var subQ4=makeQuery(id+"F16.imprint","INTERSECT",VERTEX,{"derivedFrom":[subQ1,subQ3]});Q9=makeQuery(id+"F16.imprint","IMPRINT",FACE,{"disambiguationData":[TD([[makeQuery(id+"F16.imprint","IMPRINT",EDGE,{"disambiguationData":[TD([[subQ4,-1.0]])],"derivedFrom":subQ3}),1.0]])]});}
            extrude(context, id + "F17", {"entities" : qUnion([Q0, Q1, Q2, Q3, Q4, Q5, Q6, Q7, Q8, Q9]), "operationType" : NewBodyOperationType.ADD, "depth" : 1.59 * mm, "offsetDistance" : 25.4 * mm});
        }
        {
            var Q0;
            Q0=makeQuery(id+"F13.opExtrude","CAP_FACE",FACE,{"disambiguationData":[OSD([sQuery(id+"F12.wireOp",EDGE,"E31.0.0")])],"isStart":false});
            var sketch = newSketch(context, id + "F18", { "sketchPlane" : qUnion([Q0])});
            skCircle(sketch, "E195.cCircle", {"center": v(50.8, 0) * mm, "radius": 5.08 * mm, "construction": true});
            skLineSegment(sketch, "E195.0", {"start": v(48.86, -5.97) * mm, "end": v(44.52, 0) * mm, "construction": true});
            skLineSegment(sketch, "E195.1", {"start": v(44.52, 0) * mm, "end": v(48.86, 5.97) * mm, "construction": true});
            skLineSegment(sketch, "E195.2", {"start": v(48.86, 5.97) * mm, "end": v(55.88, 3.7) * mm, "construction": true});
            skLineSegment(sketch, "E195.3", {"start": v(55.88, 3.7) * mm, "end": v(55.88, -3.7) * mm, "construction": true});
            skLineSegment(sketch, "E195.4", {"start": v(55.88, -3.7) * mm, "end": v(48.86, -5.97) * mm, "construction": true});
            skPoint(sketch, "E195.0.midPoint", {"position": v(46.7, -2.99) * mm});
            skLineSegment(sketch, "E196", {"start": v(48.86, -5.97) * mm, "end": v(37.5, -9.66) * mm});
            skLineSegment(sketch, "E197", {"start": v(37.5, -9.66) * mm, "end": v(44.52, 0) * mm});
            skLineSegment(sketch, "E198", {"start": v(44.52, 0) * mm, "end": v(37.5, 9.66) * mm});
            skLineSegment(sketch, "E199", {"start": v(37.5, 9.66) * mm, "end": v(48.86, 5.97) * mm});
            skLineSegment(sketch, "E200", {"start": v(48.86, 5.97) * mm, "end": v(55.88, 15.63) * mm});
            skLineSegment(sketch, "E201", {"start": v(55.88, 15.63) * mm, "end": v(55.88, 3.7) * mm});
            skLineSegment(sketch, "E202", {"start": v(55.88, 3.7) * mm, "end": v(67.24, 0) * mm});
            skLineSegment(sketch, "E203", {"start": v(67.24, 0) * mm, "end": v(55.88, -3.7) * mm});
            skLineSegment(sketch, "E204", {"start": v(55.88, -15.63) * mm, "end": v(48.86, -5.97) * mm});
            skLineSegment(sketch, "E205", {"start": v(55.88, -15.63) * mm, "end": v(55.88, -3.7) * mm});
            skLineSegment(sketch, "E206", {"start": v(0, 0) * mm, "end": v(0, -12.7) * mm, "construction": true});
            skLineSegment(sketch, "E207.MirrorCS", {"start": v(-48.86, -5.97) * mm, "end": v(-44.52, 0) * mm, "construction": true});
            skLineSegment(sketch, "E208.MirrorCS", {"start": v(-67.24, 0) * mm, "end": v(-55.88, -3.7) * mm});
            skLineSegment(sketch, "E209.MirrorCS", {"start": v(-48.86, -5.97) * mm, "end": v(-37.5, -9.66) * mm});
            skLineSegment(sketch, "E210.MirrorCS", {"start": v(-55.88, -15.63) * mm, "end": v(-48.86, -5.97) * mm});
            skLineSegment(sketch, "E211.MirrorCS", {"start": v(-55.88, 3.7) * mm, "end": v(-55.88, -3.7) * mm, "construction": true});
            skLineSegment(sketch, "E212.MirrorCS", {"start": v(-48.86, 5.97) * mm, "end": v(-55.88, 3.7) * mm, "construction": true});
            skLineSegment(sketch, "E213.MirrorCS", {"start": v(-55.88, -3.7) * mm, "end": v(-48.86, -5.97) * mm, "construction": true});
            skLineSegment(sketch, "E214.MirrorCS", {"start": v(-37.5, -9.66) * mm, "end": v(-44.52, 0) * mm});
            skLineSegment(sketch, "E215.MirrorCS", {"start": v(-37.5, 9.66) * mm, "end": v(-48.86, 5.97) * mm});
            skLineSegment(sketch, "E216.MirrorCS", {"start": v(-44.52, 0) * mm, "end": v(-48.86, 5.97) * mm, "construction": true});
            skPoint(sketch, "E217.MirrorP", {"position": v(-46.7, -2.99) * mm});
            skLineSegment(sketch, "E218.MirrorCS", {"start": v(-48.86, 5.97) * mm, "end": v(-55.88, 15.63) * mm});
            skLineSegment(sketch, "E219.MirrorCS", {"start": v(-44.52, 0) * mm, "end": v(-37.5, 9.66) * mm});
            skCircle(sketch, "E220.MirrorC", {"center": v(-50.8, 0) * mm, "radius": 5.08 * mm, "construction": true});
            skLineSegment(sketch, "E221.MirrorCS", {"start": v(-55.88, 3.7) * mm, "end": v(-67.24, 0) * mm});
            skLineSegment(sketch, "E222.MirrorCS", {"start": v(-55.88, -15.63) * mm, "end": v(-55.88, -3.7) * mm});
            skLineSegment(sketch, "E223.MirrorCS", {"start": v(-55.88, 15.63) * mm, "end": v(-55.88, 3.7) * mm});
            skSolve(sketch);
        }
        {
            var Q0;
            Q0=makeQuery(id+"F18.imprint","IMPRINT",FACE,{"disambiguationData":[TD([[makeQuery(id+"F18.imprint","IMPRINT",EDGE,{"derivedFrom":sQuery(id+"F18.wireOp",EDGE,"E196")}),-1.0]])]});
            var Q1;
            Q1=makeQuery(id+"F18.imprint","IMPRINT",FACE,{"disambiguationData":[TD([[makeQuery(id+"F18.imprint","IMPRINT",EDGE,{"derivedFrom":sQuery(id+"F18.wireOp",EDGE,"E208.MirrorCS")}),1.0]])]});
            extrude(context, id + "F19", {"entities" : qUnion([Q0, Q1]), "operationType" : NewBodyOperationType.ADD, "depth" : 1.59 * mm, "offsetDistance" : 25.4 * mm});
        }
    });
